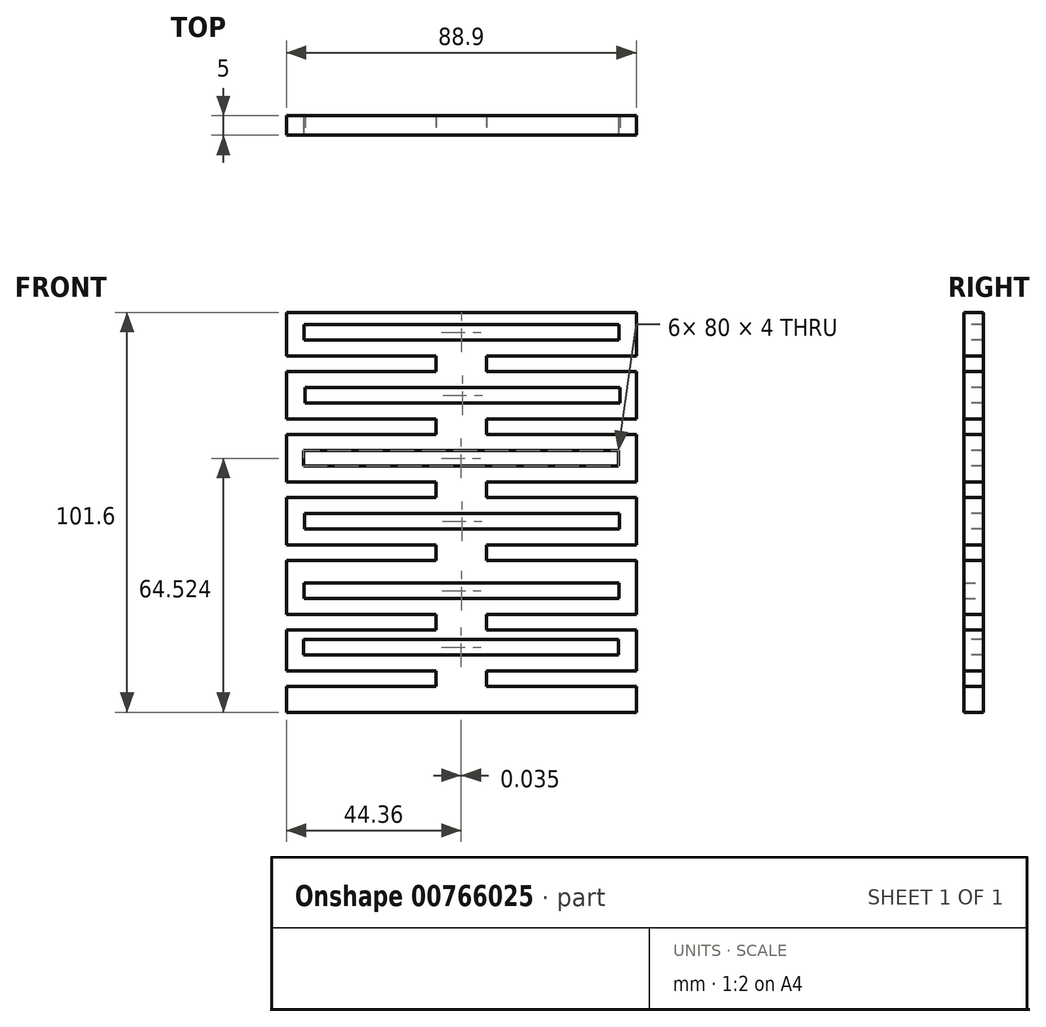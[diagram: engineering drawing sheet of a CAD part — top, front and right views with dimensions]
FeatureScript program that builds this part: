
annotation { "Feature Type Name" : "Feature", "Feature Type Description" : "" }
export const myFeature = defineFeature(function(context is Context, id is Id, definition is map)
    precondition{}
    {
        {
            var Q0;
            Q0=qCreatedBy(makeId("Front.planeOp"),FACE);
            var sketch = newSketch(context, id + "F0", { "sketchPlane" : qUnion([Q0])});
            skLineSegment(sketch, "E0.bottom", {"start": v(-43.64, 45.99) * mm, "end": v(45.26, 45.99) * mm});
            skLineSegment(sketch, "E0.top", {"start": v(-43.64, -55.61) * mm, "end": v(45.26, -55.61) * mm});
            skLineSegment(sketch, "E0.left", {"start": v(-43.64, 45.99) * mm, "end": v(-43.64, -55.61) * mm});
            skLineSegment(sketch, "E0.right", {"start": v(45.26, 45.99) * mm, "end": v(45.26, -55.61) * mm});
            skLineSegment(sketch, "E1", {"start": v(0.8, 45.99) * mm, "end": v(0.8, -55.61) * mm});
            skLineSegment(sketch, "E2.bottom", {"start": v(-38.37, 41.45) * mm, "end": v(41.63, 41.45) * mm});
            skLineSegment(sketch, "E2.top", {"start": v(-38.37, 37.95) * mm, "end": v(41.63, 37.95) * mm});
            skLineSegment(sketch, "E2.left", {"start": v(-38.37, 41.45) * mm, "end": v(-38.37, 37.95) * mm});
            skLineSegment(sketch, "E2.right", {"start": v(41.63, 41.45) * mm, "end": v(41.63, 37.95) * mm});
            skSolve(sketch);
        }
        {
            var Q0;
            {var subQ5=sQuery(id+"F0.wireOp",EDGE,"E0.left");Q0=makeQuery(id+"F0.imprint","IMPRINT",FACE,{"disambiguationData":[TD([[makeQuery(id+"F0.imprint","IMPRINT",EDGE,{"derivedFrom":subQ5}),1.0]])]});}
            var Q1;
            {var subQ0=sQuery(id+"F0.wireOp",EDGE,"E0.right");Q1=makeQuery(id+"F0.imprint","IMPRINT",FACE,{"disambiguationData":[TD([[makeQuery(id+"F0.imprint","IMPRINT",EDGE,{"derivedFrom":subQ0}),-1.0]])]});}
            var Q2;
            {var subQ5=sQuery(id+"F0.wireOp",EDGE,"E2.left");Q2=makeQuery(id+"F0.imprint","IMPRINT",FACE,{"disambiguationData":[TD([[makeQuery(id+"F0.imprint","IMPRINT",EDGE,{"derivedFrom":subQ5}),1.0]])]});}
            var Q3;
            {var subQ5=sQuery(id+"F0.wireOp",EDGE,"E2.right");Q3=makeQuery(id+"F0.imprint","IMPRINT",FACE,{"disambiguationData":[TD([[makeQuery(id+"F0.imprint","IMPRINT",EDGE,{"derivedFrom":subQ5}),-1.0]])]});}
            extrude(context, id + "F1", {"entities" : qUnion([Q0, Q1, Q2, Q3]), "depth" : 5 * mm, "offsetDistance" : 25 * mm});
        }
        {
            var Q0;
            Q0=makeQuery(id+"F1.opExtrude","CAP_FACE",FACE,{"disambiguationData":[OSD([sQuery(id+"F0.wireOp",EDGE,"E0.bottom"),sQuery(id+"F0.wireOp",EDGE,"E0.top"),sQuery(id+"F0.wireOp",EDGE,"E0.left"),sQuery(id+"F0.wireOp",EDGE,"E0.right")])],"isStart":false});
            var sketch = newSketch(context, id + "F2", { "sketchPlane" : qUnion([Q0])});
            skLineSegment(sketch, "E3.bottom", {"start": v(-39.2, 42.91) * mm, "end": v(40.8, 42.91) * mm});
            skLineSegment(sketch, "E3.top", {"start": v(-39.2, 38.91) * mm, "end": v(40.8, 38.91) * mm});
            skLineSegment(sketch, "E3.left", {"start": v(-39.2, 42.91) * mm, "end": v(-39.2, 38.91) * mm});
            skLineSegment(sketch, "E3.right", {"start": v(40.8, 42.91) * mm, "end": v(40.8, 38.91) * mm});
            skLineSegment(sketch, "E4.bottom", {"start": v(-43.64, 34.91) * mm, "end": v(-5.64, 34.91) * mm});
            skLineSegment(sketch, "E4.top", {"start": v(-43.64, 30.91) * mm, "end": v(-5.64, 30.91) * mm});
            skLineSegment(sketch, "E4.left", {"start": v(-43.64, 34.91) * mm, "end": v(-43.64, 30.91) * mm});
            skLineSegment(sketch, "E4.right", {"start": v(-5.64, 34.91) * mm, "end": v(-5.64, 30.91) * mm});
            skLineSegment(sketch, "E5.bottom", {"start": v(7.26, 34.91) * mm, "end": v(45.26, 34.91) * mm});
            skLineSegment(sketch, "E5.top", {"start": v(7.26, 30.91) * mm, "end": v(45.26, 30.91) * mm});
            skLineSegment(sketch, "E5.left", {"start": v(7.26, 34.91) * mm, "end": v(7.26, 30.91) * mm});
            skLineSegment(sketch, "E5.right", {"start": v(45.26, 34.91) * mm, "end": v(45.26, 30.91) * mm});
            skLineSegment(sketch, "E6.bottom", {"start": v(-38.85, 26.91) * mm, "end": v(41.15, 26.91) * mm});
            skLineSegment(sketch, "E6.top", {"start": v(-38.85, 22.91) * mm, "end": v(41.15, 22.91) * mm});
            skLineSegment(sketch, "E6.left", {"start": v(-38.85, 26.91) * mm, "end": v(-38.85, 22.91) * mm});
            skLineSegment(sketch, "E6.right", {"start": v(41.15, 26.91) * mm, "end": v(41.15, 22.91) * mm});
            skLineSegment(sketch, "E7.bottom", {"start": v(-38.85, 26.91) * mm, "end": v(-38.85, 26.91) * mm});
            skLineSegment(sketch, "E7.top", {"start": v(-38.85, 34.91) * mm, "end": v(-38.85, 34.91) * mm});
            skLineSegment(sketch, "E7.left", {"start": v(-38.85, 26.91) * mm, "end": v(-38.85, 34.91) * mm});
            skLineSegment(sketch, "E7.right", {"start": v(-38.85, 26.91) * mm, "end": v(-38.85, 34.91) * mm});
            skLineSegment(sketch, "E8.bottom", {"start": v(-43.64, 18.91) * mm, "end": v(-5.64, 18.91) * mm});
            skLineSegment(sketch, "E8.top", {"start": v(-43.64, 14.91) * mm, "end": v(-5.64, 14.91) * mm});
            skLineSegment(sketch, "E8.left", {"start": v(-43.64, 18.91) * mm, "end": v(-43.64, 14.91) * mm});
            skLineSegment(sketch, "E8.right", {"start": v(-5.64, 18.91) * mm, "end": v(-5.64, 14.91) * mm});
            skLineSegment(sketch, "E9.bottom", {"start": v(7.26, 18.91) * mm, "end": v(45.26, 18.91) * mm});
            skLineSegment(sketch, "E9.top", {"start": v(7.26, 14.91) * mm, "end": v(45.26, 14.91) * mm});
            skLineSegment(sketch, "E9.left", {"start": v(7.26, 18.91) * mm, "end": v(7.26, 14.91) * mm});
            skLineSegment(sketch, "E9.right", {"start": v(45.26, 18.91) * mm, "end": v(45.26, 14.91) * mm});
            skLineSegment(sketch, "E10.bottom", {"start": v(-39.28, 10.91) * mm, "end": v(40.72, 10.91) * mm});
            skLineSegment(sketch, "E10.top", {"start": v(-39.28, 6.91) * mm, "end": v(40.72, 6.91) * mm});
            skLineSegment(sketch, "E10.left", {"start": v(-39.28, 10.91) * mm, "end": v(-39.28, 6.91) * mm});
            skLineSegment(sketch, "E10.right", {"start": v(40.72, 10.91) * mm, "end": v(40.72, 6.91) * mm});
            skLineSegment(sketch, "E11.bottom", {"start": v(-43.64, 2.91) * mm, "end": v(-5.64, 2.91) * mm});
            skLineSegment(sketch, "E11.top", {"start": v(-43.64, -1.09) * mm, "end": v(-5.64, -1.09) * mm});
            skLineSegment(sketch, "E11.left", {"start": v(-43.64, 2.91) * mm, "end": v(-43.64, -1.09) * mm});
            skLineSegment(sketch, "E11.right", {"start": v(-5.64, 2.91) * mm, "end": v(-5.64, -1.09) * mm});
            skLineSegment(sketch, "E12.bottom", {"start": v(7.26, 2.91) * mm, "end": v(45.26, 2.91) * mm});
            skLineSegment(sketch, "E12.top", {"start": v(7.26, -1.09) * mm, "end": v(45.26, -1.09) * mm});
            skLineSegment(sketch, "E12.left", {"start": v(7.26, 2.91) * mm, "end": v(7.26, -1.09) * mm});
            skLineSegment(sketch, "E12.right", {"start": v(45.26, 2.91) * mm, "end": v(45.26, -1.09) * mm});
            skLineSegment(sketch, "E13.bottom", {"start": v(-38.99, -5.09) * mm, "end": v(41.01, -5.09) * mm});
            skLineSegment(sketch, "E13.top", {"start": v(-38.99, -9.09) * mm, "end": v(41.01, -9.09) * mm});
            skLineSegment(sketch, "E13.left", {"start": v(-38.99, -5.09) * mm, "end": v(-38.99, -9.09) * mm});
            skLineSegment(sketch, "E13.right", {"start": v(41.01, -5.09) * mm, "end": v(41.01, -9.09) * mm});
            skLineSegment(sketch, "E14.bottom", {"start": v(-43.64, -13.09) * mm, "end": v(-5.64, -13.09) * mm});
            skLineSegment(sketch, "E14.top", {"start": v(-43.64, -17.09) * mm, "end": v(-5.64, -17.09) * mm});
            skLineSegment(sketch, "E14.left", {"start": v(-43.64, -13.09) * mm, "end": v(-43.64, -17.09) * mm});
            skLineSegment(sketch, "E14.right", {"start": v(-5.64, -13.09) * mm, "end": v(-5.64, -17.09) * mm});
            skLineSegment(sketch, "E15.bottom", {"start": v(7.26, -13.09) * mm, "end": v(45.26, -13.09) * mm});
            skLineSegment(sketch, "E15.top", {"start": v(7.26, -17.09) * mm, "end": v(45.26, -17.09) * mm});
            skLineSegment(sketch, "E15.left", {"start": v(7.26, -13.09) * mm, "end": v(7.26, -17.09) * mm});
            skLineSegment(sketch, "E15.right", {"start": v(45.26, -13.09) * mm, "end": v(45.26, -17.09) * mm});
            skLineSegment(sketch, "E16.bottom", {"start": v(-41.68, -21.09) * mm, "end": v(38.32, -21.09) * mm});
            skLineSegment(sketch, "E16.top", {"start": v(-41.68, -25.09) * mm, "end": v(38.32, -25.09) * mm});
            skLineSegment(sketch, "E16.left", {"start": v(-41.68, -21.09) * mm, "end": v(-41.68, -25.09) * mm});
            skLineSegment(sketch, "E16.right", {"start": v(38.32, -21.09) * mm, "end": v(38.32, -25.09) * mm});
            skLineSegment(sketch, "E17.bottom", {"start": v(-43.64, -29.09) * mm, "end": v(-5.64, -29.09) * mm});
            skLineSegment(sketch, "E17.top", {"start": v(-43.64, -33.09) * mm, "end": v(-5.64, -33.09) * mm});
            skLineSegment(sketch, "E17.left", {"start": v(-43.64, -29.09) * mm, "end": v(-43.64, -33.09) * mm});
            skLineSegment(sketch, "E17.right", {"start": v(-5.64, -29.09) * mm, "end": v(-5.64, -33.09) * mm});
            skLineSegment(sketch, "E18.bottom", {"start": v(7.26, -29.09) * mm, "end": v(45.26, -29.09) * mm});
            skLineSegment(sketch, "E18.top", {"start": v(7.26, -33.09) * mm, "end": v(45.26, -33.09) * mm});
            skLineSegment(sketch, "E18.left", {"start": v(7.26, -29.09) * mm, "end": v(7.26, -33.09) * mm});
            skLineSegment(sketch, "E18.right", {"start": v(45.26, -29.09) * mm, "end": v(45.26, -33.09) * mm});
            skLineSegment(sketch, "E19.bottom", {"start": v(-39.24, -37.09) * mm, "end": v(40.76, -37.09) * mm});
            skLineSegment(sketch, "E19.top", {"start": v(-39.24, -41.09) * mm, "end": v(40.76, -41.09) * mm});
            skLineSegment(sketch, "E19.left", {"start": v(-39.24, -37.09) * mm, "end": v(-39.24, -41.09) * mm});
            skLineSegment(sketch, "E19.right", {"start": v(40.76, -37.09) * mm, "end": v(40.76, -41.09) * mm});
            skLineSegment(sketch, "E20.bottom", {"start": v(-43.64, -45.09) * mm, "end": v(-5.64, -45.09) * mm});
            skLineSegment(sketch, "E20.top", {"start": v(-43.64, -49.09) * mm, "end": v(-5.64, -49.09) * mm});
            skLineSegment(sketch, "E20.left", {"start": v(-43.64, -45.09) * mm, "end": v(-43.64, -49.09) * mm});
            skLineSegment(sketch, "E20.right", {"start": v(-5.64, -45.09) * mm, "end": v(-5.64, -49.09) * mm});
            skLineSegment(sketch, "E21.bottom", {"start": v(7.26, -45.09) * mm, "end": v(45.26, -45.09) * mm});
            skLineSegment(sketch, "E21.top", {"start": v(7.26, -49.09) * mm, "end": v(45.26, -49.09) * mm});
            skLineSegment(sketch, "E21.left", {"start": v(7.26, -45.09) * mm, "end": v(7.26, -49.09) * mm});
            skLineSegment(sketch, "E21.right", {"start": v(45.26, -45.09) * mm, "end": v(45.26, -49.09) * mm});
            skSolve(sketch);
        }
        {
            var Q0;
            Q0=makeQuery(id+"F2.imprint","IMPRINT",FACE,{"disambiguationData":[TD([[makeQuery(id+"F2.imprint","IMPRINT",EDGE,{"derivedFrom":sQuery(id+"F2.wireOp",EDGE,"E10.bottom")}),-1.0]])]});
            var Q1;
            Q1=makeQuery(id+"F2.imprint","IMPRINT",FACE,{"disambiguationData":[TD([[makeQuery(id+"F2.imprint","IMPRINT",EDGE,{"derivedFrom":sQuery(id+"F2.wireOp",EDGE,"E6.bottom")}),-1.0]])]});
            var Q2;
            Q2=makeQuery(id+"F2.imprint","IMPRINT",FACE,{"disambiguationData":[TD([[makeQuery(id+"F2.imprint","IMPRINT",EDGE,{"derivedFrom":sQuery(id+"F2.wireOp",EDGE,"E19.bottom")}),-1.0]])]});
            var Q3;
            Q3=makeQuery(id+"F2.imprint","IMPRINT",FACE,{"disambiguationData":[TD([[makeQuery(id+"F2.imprint","IMPRINT",EDGE,{"derivedFrom":sQuery(id+"F2.wireOp",EDGE,"E3.bottom")}),-1.0]])]});
            var Q4;
            Q4=makeQuery(id+"F2.imprint","IMPRINT",FACE,{"disambiguationData":[TD([[makeQuery(id+"F2.imprint","IMPRINT",EDGE,{"derivedFrom":sQuery(id+"F2.wireOp",EDGE,"E13.bottom")}),-1.0]])]});
            var Q5;
            {var subQ0=sQuery(id+"F2.wireOp",EDGE,"E4.right");Q5=makeQuery(id+"F2.imprint","IMPRINT",FACE,{"disambiguationData":[TD([[makeQuery(id+"F2.imprint","IMPRINT",EDGE,{"derivedFrom":subQ0}),-1.0]])]});}
            extrude(context, id + "F3", {"entities" : qUnion([Q0, Q1, Q2, Q3, Q4, Q5]), "operationType" : NewBodyOperationType.REMOVE, "oppositeDirection" : true, "depth" : 12 * mm, "offsetDistance" : 25 * mm});
        }
        {
            var Q0;
            Q0=makeQuery(id+"F1.opExtrude","CAP_FACE",FACE,{"disambiguationData":[OSD([sQuery(id+"F0.wireOp",EDGE,"E0.bottom"),sQuery(id+"F0.wireOp",EDGE,"E0.top"),sQuery(id+"F0.wireOp",EDGE,"E0.left"),sQuery(id+"F0.wireOp",EDGE,"E0.right")])],"isStart":false});
            var sketch = newSketch(context, id + "F4", { "sketchPlane" : qUnion([Q0])});
            skLineSegment(sketch, "E22.bottom", {"start": v(-43.64, 34.91) * mm, "end": v(-36.2, 34.91) * mm});
            skLineSegment(sketch, "E22.top", {"start": v(-43.64, 30.91) * mm, "end": v(-36.2, 30.91) * mm});
            skLineSegment(sketch, "E22.left", {"start": v(-43.64, 34.91) * mm, "end": v(-43.64, 30.91) * mm});
            skLineSegment(sketch, "E22.right", {"start": v(-36.2, 34.91) * mm, "end": v(-36.2, 30.91) * mm});
            skSolve(sketch);
        }
        {
            var Q0;
            Q0 = qSketchRegion(id + "F4", true);
            extrude(context, id + "F5", {"entities" : qUnion([Q0]), "operationType" : NewBodyOperationType.REMOVE, "oppositeDirection" : true, "depth" : 12 * mm, "offsetDistance" : 25 * mm});
        }
        {
            var Q0;
            Q0=makeQuery(id+"F1.opExtrude","CAP_FACE",FACE,{"disambiguationData":[OSD([sQuery(id+"F0.wireOp",EDGE,"E0.bottom"),sQuery(id+"F0.wireOp",EDGE,"E0.top"),sQuery(id+"F0.wireOp",EDGE,"E0.left"),sQuery(id+"F0.wireOp",EDGE,"E0.right")])],"isStart":false});
            var sketch = newSketch(context, id + "F6", { "sketchPlane" : qUnion([Q0])});
            skLineSegment(sketch, "E23.bottom", {"start": v(7.26, 34.91) * mm, "end": v(45.26, 34.91) * mm});
            skLineSegment(sketch, "E23.top", {"start": v(7.26, 30.91) * mm, "end": v(45.26, 30.91) * mm});
            skLineSegment(sketch, "E23.left", {"start": v(7.26, 34.91) * mm, "end": v(7.26, 30.91) * mm});
            skLineSegment(sketch, "E23.right", {"start": v(45.26, 34.91) * mm, "end": v(45.26, 30.91) * mm});
            skSolve(sketch);
        }
        {
            var Q0;
            Q0=makeQuery(id+"F6.imprint","IMPRINT",FACE,{"disambiguationData":[TD([[makeQuery(id+"F6.imprint","IMPRINT",EDGE,{"derivedFrom":sQuery(id+"F6.wireOp",EDGE,"E23.bottom")}),-1.0]])]});
            extrude(context, id + "F7", {"entities" : qUnion([Q0]), "operationType" : NewBodyOperationType.REMOVE, "oppositeDirection" : true, "depth" : 12 * mm, "offsetDistance" : 25 * mm});
        }
        {
            var Q0;
            Q0=makeQuery(id+"F1.opExtrude","CAP_FACE",FACE,{"disambiguationData":[OSD([sQuery(id+"F0.wireOp",EDGE,"E0.bottom"),sQuery(id+"F0.wireOp",EDGE,"E0.top"),sQuery(id+"F0.wireOp",EDGE,"E0.left"),sQuery(id+"F0.wireOp",EDGE,"E0.right")])],"isStart":false});
            var sketch = newSketch(context, id + "F8", { "sketchPlane" : qUnion([Q0])});
            skLineSegment(sketch, "E24.bottom", {"start": v(-43.64, 18.91) * mm, "end": v(-5.64, 18.91) * mm});
            skLineSegment(sketch, "E24.top", {"start": v(-43.64, 14.91) * mm, "end": v(-5.64, 14.91) * mm});
            skLineSegment(sketch, "E24.left", {"start": v(-43.64, 18.91) * mm, "end": v(-43.64, 14.91) * mm});
            skLineSegment(sketch, "E24.right", {"start": v(-5.64, 18.91) * mm, "end": v(-5.64, 14.91) * mm});
            skSolve(sketch);
        }
        {
            var Q0;
            Q0 = qSketchRegion(id + "F8", true);
            extrude(context, id + "F9", {"entities" : qUnion([Q0]), "operationType" : NewBodyOperationType.REMOVE, "oppositeDirection" : true, "depth" : 12 * mm, "offsetDistance" : 25 * mm});
        }
        {
            var Q0;
            Q0=makeQuery(id+"F1.opExtrude","CAP_FACE",FACE,{"disambiguationData":[OSD([sQuery(id+"F0.wireOp",EDGE,"E0.bottom"),sQuery(id+"F0.wireOp",EDGE,"E0.top"),sQuery(id+"F0.wireOp",EDGE,"E0.left"),sQuery(id+"F0.wireOp",EDGE,"E0.right")])],"isStart":false});
            var sketch = newSketch(context, id + "F10", { "sketchPlane" : qUnion([Q0])});
            skLineSegment(sketch, "E25.bottom", {"start": v(7.26, 18.91) * mm, "end": v(45.26, 18.91) * mm});
            skLineSegment(sketch, "E25.top", {"start": v(7.26, 14.91) * mm, "end": v(45.26, 14.91) * mm});
            skLineSegment(sketch, "E25.left", {"start": v(7.26, 18.91) * mm, "end": v(7.26, 14.91) * mm});
            skLineSegment(sketch, "E25.right", {"start": v(45.26, 18.91) * mm, "end": v(45.26, 14.91) * mm});
            skSolve(sketch);
        }
        {
            var Q0;
            Q0=makeQuery(id+"F10.imprint","IMPRINT",FACE,{"disambiguationData":[TD([[makeQuery(id+"F10.imprint","IMPRINT",EDGE,{"derivedFrom":sQuery(id+"F10.wireOp",EDGE,"E25.bottom")}),-1.0]])]});
            extrude(context, id + "F11", {"entities" : qUnion([Q0]), "operationType" : NewBodyOperationType.REMOVE, "oppositeDirection" : true, "depth" : 12 * mm, "offsetDistance" : 25 * mm});
        }
        {
            var Q0;
            Q0=makeQuery(id+"F1.opExtrude","CAP_FACE",FACE,{"disambiguationData":[OSD([sQuery(id+"F0.wireOp",EDGE,"E0.bottom"),sQuery(id+"F0.wireOp",EDGE,"E0.top"),sQuery(id+"F0.wireOp",EDGE,"E0.left"),sQuery(id+"F0.wireOp",EDGE,"E0.right")])],"isStart":false});
            var sketch = newSketch(context, id + "F12", { "sketchPlane" : qUnion([Q0])});
            skLineSegment(sketch, "E26.bottom", {"start": v(-43.64, 2.91) * mm, "end": v(-5.64, 2.91) * mm});
            skLineSegment(sketch, "E26.top", {"start": v(-43.64, -1.09) * mm, "end": v(-5.64, -1.09) * mm});
            skLineSegment(sketch, "E26.left", {"start": v(-43.64, 2.91) * mm, "end": v(-43.64, -1.09) * mm});
            skLineSegment(sketch, "E26.right", {"start": v(-5.64, 2.91) * mm, "end": v(-5.64, -1.09) * mm});
            skSolve(sketch);
        }
        {
            var Q0;
            Q0=makeQuery(id+"F12.imprint","IMPRINT",FACE,{"disambiguationData":[TD([[makeQuery(id+"F12.imprint","IMPRINT",EDGE,{"derivedFrom":sQuery(id+"F12.wireOp",EDGE,"E26.bottom")}),-1.0]])]});
            extrude(context, id + "F13", {"entities" : qUnion([Q0]), "operationType" : NewBodyOperationType.REMOVE, "oppositeDirection" : true, "depth" : 12 * mm, "offsetDistance" : 25 * mm});
        }
        {
            var Q0;
            Q0=makeQuery(id+"F1.opExtrude","CAP_FACE",FACE,{"disambiguationData":[OSD([sQuery(id+"F0.wireOp",EDGE,"E0.bottom"),sQuery(id+"F0.wireOp",EDGE,"E0.top"),sQuery(id+"F0.wireOp",EDGE,"E0.left"),sQuery(id+"F0.wireOp",EDGE,"E0.right")])],"isStart":true});
            var sketch = newSketch(context, id + "F14", { "sketchPlane" : qUnion([Q0])});
            skLineSegment(sketch, "E27.bottom", {"start": v(-45.26, 2.91) * mm, "end": v(-7.26, 2.91) * mm});
            skLineSegment(sketch, "E27.top", {"start": v(-45.26, -1.09) * mm, "end": v(-7.26, -1.09) * mm});
            skLineSegment(sketch, "E27.left", {"start": v(-45.26, 2.91) * mm, "end": v(-45.26, -1.09) * mm});
            skLineSegment(sketch, "E27.right", {"start": v(-7.26, 2.91) * mm, "end": v(-7.26, -1.09) * mm});
            skSolve(sketch);
        }
        {
            var Q0;
            Q0=makeQuery(id+"F14.imprint","IMPRINT",FACE,{"disambiguationData":[TD([[makeQuery(id+"F14.imprint","IMPRINT",EDGE,{"derivedFrom":sQuery(id+"F14.wireOp",EDGE,"E27.bottom")}),-1.0]])]});
            extrude(context, id + "F15", {"entities" : qUnion([Q0]), "operationType" : NewBodyOperationType.REMOVE, "oppositeDirection" : true, "depth" : 12 * mm, "offsetDistance" : 25 * mm});
        }
        {
            var Q0;
            Q0=makeQuery(id+"F1.opExtrude","CAP_FACE",FACE,{"disambiguationData":[OSD([sQuery(id+"F0.wireOp",EDGE,"E0.bottom"),sQuery(id+"F0.wireOp",EDGE,"E0.top"),sQuery(id+"F0.wireOp",EDGE,"E0.left"),sQuery(id+"F0.wireOp",EDGE,"E0.right")])],"isStart":true});
            var sketch = newSketch(context, id + "F16", { "sketchPlane" : qUnion([Q0])});
            skLineSegment(sketch, "E28.bottom", {"start": v(-45.26, -13.09) * mm, "end": v(-7.26, -13.09) * mm});
            skLineSegment(sketch, "E28.top", {"start": v(-45.26, -17.09) * mm, "end": v(-7.26, -17.09) * mm});
            skLineSegment(sketch, "E28.left", {"start": v(-45.26, -13.09) * mm, "end": v(-45.26, -17.09) * mm});
            skLineSegment(sketch, "E28.right", {"start": v(-7.26, -13.09) * mm, "end": v(-7.26, -17.09) * mm});
            skSolve(sketch);
        }
        {
            var Q0;
            Q0=makeQuery(id+"F16.imprint","IMPRINT",FACE,{"disambiguationData":[TD([[makeQuery(id+"F16.imprint","IMPRINT",EDGE,{"derivedFrom":sQuery(id+"F16.wireOp",EDGE,"E28.bottom")}),-1.0]])]});
            extrude(context, id + "F17", {"entities" : qUnion([Q0]), "operationType" : NewBodyOperationType.REMOVE, "oppositeDirection" : true, "depth" : 12 * mm, "offsetDistance" : 25 * mm});
        }
        {
            var Q0;
            Q0=makeQuery(id+"F1.opExtrude","CAP_FACE",FACE,{"disambiguationData":[OSD([sQuery(id+"F0.wireOp",EDGE,"E0.bottom"),sQuery(id+"F0.wireOp",EDGE,"E0.top"),sQuery(id+"F0.wireOp",EDGE,"E0.left"),sQuery(id+"F0.wireOp",EDGE,"E0.right")])],"isStart":true});
            var sketch = newSketch(context, id + "F18", { "sketchPlane" : qUnion([Q0])});
            skLineSegment(sketch, "E29.bottom", {"start": v(5.64, -13.09) * mm, "end": v(43.64, -13.09) * mm});
            skLineSegment(sketch, "E29.top", {"start": v(5.64, -17.09) * mm, "end": v(43.64, -17.09) * mm});
            skLineSegment(sketch, "E29.left", {"start": v(5.64, -13.09) * mm, "end": v(5.64, -17.09) * mm});
            skLineSegment(sketch, "E29.right", {"start": v(43.64, -13.09) * mm, "end": v(43.64, -17.09) * mm});
            skSolve(sketch);
        }
        {
            var Q0;
            Q0 = qSketchRegion(id + "F18", true);
            var Q1;
            Q1=makeQuery(id+"F18.imprint","IMPRINT",FACE,{"disambiguationData":[TD([[makeQuery(id+"F18.imprint","IMPRINT",EDGE,{"derivedFrom":sQuery(id+"F18.wireOp",EDGE,"E29.bottom")}),-1.0]])]});
            extrude(context, id + "F19", {"entities" : qUnion([Q0, Q1]), "operationType" : NewBodyOperationType.REMOVE, "oppositeDirection" : true, "depth" : 12 * mm, "offsetDistance" : 25 * mm});
        }
        {
            var Q0;
            Q0=makeQuery(id+"F1.opExtrude","CAP_FACE",FACE,{"disambiguationData":[OSD([sQuery(id+"F0.wireOp",EDGE,"E0.bottom"),sQuery(id+"F0.wireOp",EDGE,"E0.top"),sQuery(id+"F0.wireOp",EDGE,"E0.left"),sQuery(id+"F0.wireOp",EDGE,"E0.right")])],"isStart":true});
            var sketch = newSketch(context, id + "F20", { "sketchPlane" : qUnion([Q0])});
            skLineSegment(sketch, "E30.bottom", {"start": v(-40.86, -22.76) * mm, "end": v(39.14, -22.76) * mm});
            skLineSegment(sketch, "E30.top", {"start": v(-40.86, -26.76) * mm, "end": v(39.14, -26.76) * mm});
            skLineSegment(sketch, "E30.left", {"start": v(-40.86, -22.76) * mm, "end": v(-40.86, -26.76) * mm});
            skLineSegment(sketch, "E30.right", {"start": v(39.14, -22.76) * mm, "end": v(39.14, -26.76) * mm});
            skSolve(sketch);
        }
        {
            var Q0;
            Q0=makeQuery(id+"F20.imprint","IMPRINT",FACE,{"disambiguationData":[TD([[makeQuery(id+"F20.imprint","IMPRINT",EDGE,{"derivedFrom":sQuery(id+"F20.wireOp",EDGE,"E30.bottom")}),-1.0]])]});
            extrude(context, id + "F21", {"entities" : qUnion([Q0]), "operationType" : NewBodyOperationType.REMOVE, "oppositeDirection" : true, "depth" : 12 * mm, "offsetDistance" : 25 * mm});
        }
        {
            var Q0;
            Q0=makeQuery(id+"F1.opExtrude","CAP_FACE",FACE,{"disambiguationData":[OSD([sQuery(id+"F0.wireOp",EDGE,"E0.bottom"),sQuery(id+"F0.wireOp",EDGE,"E0.top"),sQuery(id+"F0.wireOp",EDGE,"E0.left"),sQuery(id+"F0.wireOp",EDGE,"E0.right")])],"isStart":true});
            var sketch = newSketch(context, id + "F22", { "sketchPlane" : qUnion([Q0])});
            skLineSegment(sketch, "E31.bottom", {"start": v(-45.26, -30.76) * mm, "end": v(-7.26, -30.76) * mm});
            skLineSegment(sketch, "E31.top", {"start": v(-45.26, -34.76) * mm, "end": v(-7.26, -34.76) * mm});
            skLineSegment(sketch, "E31.left", {"start": v(-45.26, -30.76) * mm, "end": v(-45.26, -34.76) * mm});
            skLineSegment(sketch, "E31.right", {"start": v(-7.26, -30.76) * mm, "end": v(-7.26, -34.76) * mm});
            skSolve(sketch);
        }
        {
            var Q0;
            Q0=makeQuery(id+"F22.imprint","IMPRINT",FACE,{"disambiguationData":[TD([[makeQuery(id+"F22.imprint","IMPRINT",EDGE,{"derivedFrom":sQuery(id+"F22.wireOp",EDGE,"E31.bottom")}),-1.0]])]});
            extrude(context, id + "F23", {"entities" : qUnion([Q0]), "operationType" : NewBodyOperationType.REMOVE, "oppositeDirection" : true, "depth" : 12 * mm, "offsetDistance" : 25 * mm});
        }
        {
            var Q0;
            Q0=makeQuery(id+"F1.opExtrude","CAP_FACE",FACE,{"disambiguationData":[OSD([sQuery(id+"F0.wireOp",EDGE,"E0.bottom"),sQuery(id+"F0.wireOp",EDGE,"E0.top"),sQuery(id+"F0.wireOp",EDGE,"E0.left"),sQuery(id+"F0.wireOp",EDGE,"E0.right")])],"isStart":true});
            var sketch = newSketch(context, id + "F24", { "sketchPlane" : qUnion([Q0])});
            skLineSegment(sketch, "E32.bottom", {"start": v(5.64, -30.76) * mm, "end": v(43.64, -30.76) * mm});
            skLineSegment(sketch, "E32.top", {"start": v(5.64, -34.76) * mm, "end": v(43.64, -34.76) * mm});
            skLineSegment(sketch, "E32.left", {"start": v(5.64, -30.76) * mm, "end": v(5.64, -34.76) * mm});
            skLineSegment(sketch, "E32.right", {"start": v(43.64, -30.76) * mm, "end": v(43.64, -34.76) * mm});
            skSolve(sketch);
        }
        {
            var Q0;
            Q0=makeQuery(id+"F24.imprint","IMPRINT",FACE,{"disambiguationData":[TD([[makeQuery(id+"F24.imprint","IMPRINT",EDGE,{"derivedFrom":sQuery(id+"F24.wireOp",EDGE,"E32.bottom")}),-1.0]])]});
            extrude(context, id + "F25", {"entities" : qUnion([Q0]), "operationType" : NewBodyOperationType.REMOVE, "oppositeDirection" : true, "depth" : 12 * mm, "offsetDistance" : 25 * mm});
        }
        {
            var Q0;
            Q0=makeQuery(id+"F1.opExtrude","CAP_FACE",FACE,{"disambiguationData":[OSD([sQuery(id+"F0.wireOp",EDGE,"E0.bottom"),sQuery(id+"F0.wireOp",EDGE,"E0.top"),sQuery(id+"F0.wireOp",EDGE,"E0.left"),sQuery(id+"F0.wireOp",EDGE,"E0.right")])],"isStart":false});
            var sketch = newSketch(context, id + "F26", { "sketchPlane" : qUnion([Q0])});
            skLineSegment(sketch, "E33.bottom", {"start": v(-43.64, -45.09) * mm, "end": v(-5.64, -45.09) * mm});
            skLineSegment(sketch, "E33.top", {"start": v(-43.64, -49.09) * mm, "end": v(-5.64, -49.09) * mm});
            skLineSegment(sketch, "E33.left", {"start": v(-43.64, -45.09) * mm, "end": v(-43.64, -49.09) * mm});
            skLineSegment(sketch, "E33.right", {"start": v(-5.64, -45.09) * mm, "end": v(-5.64, -49.09) * mm});
            skSolve(sketch);
        }
        {
            var Q0;
            Q0=makeQuery(id+"F26.imprint","IMPRINT",FACE,{"disambiguationData":[TD([[makeQuery(id+"F26.imprint","IMPRINT",EDGE,{"derivedFrom":sQuery(id+"F26.wireOp",EDGE,"E33.bottom")}),-1.0]])]});
            extrude(context, id + "F27", {"entities" : qUnion([Q0]), "operationType" : NewBodyOperationType.REMOVE, "oppositeDirection" : true, "depth" : 25 * mm, "offsetDistance" : 25 * mm});
        }
        {
            var Q0;
            Q0=makeQuery(id+"F1.opExtrude","CAP_FACE",FACE,{"disambiguationData":[OSD([sQuery(id+"F0.wireOp",EDGE,"E0.bottom"),sQuery(id+"F0.wireOp",EDGE,"E0.top"),sQuery(id+"F0.wireOp",EDGE,"E0.left"),sQuery(id+"F0.wireOp",EDGE,"E0.right")])],"isStart":false});
            var sketch = newSketch(context, id + "F28", { "sketchPlane" : qUnion([Q0])});
            skLineSegment(sketch, "E34.bottom", {"start": v(7.26, -45.09) * mm, "end": v(45.26, -45.09) * mm});
            skLineSegment(sketch, "E34.top", {"start": v(7.26, -49.09) * mm, "end": v(45.26, -49.09) * mm});
            skLineSegment(sketch, "E34.left", {"start": v(7.26, -45.09) * mm, "end": v(7.26, -49.09) * mm});
            skLineSegment(sketch, "E34.right", {"start": v(45.26, -45.09) * mm, "end": v(45.26, -49.09) * mm});
            skSolve(sketch);
        }
        {
            var Q0;
            Q0=makeQuery(id+"F28.imprint","IMPRINT",FACE,{"disambiguationData":[TD([[makeQuery(id+"F28.imprint","IMPRINT",EDGE,{"derivedFrom":sQuery(id+"F28.wireOp",EDGE,"E34.bottom")}),-1.0]])]});
            extrude(context, id + "F29", {"entities" : qUnion([Q0]), "operationType" : NewBodyOperationType.REMOVE, "oppositeDirection" : true, "depth" : 25 * mm, "offsetDistance" : 25 * mm});
        }
    });
